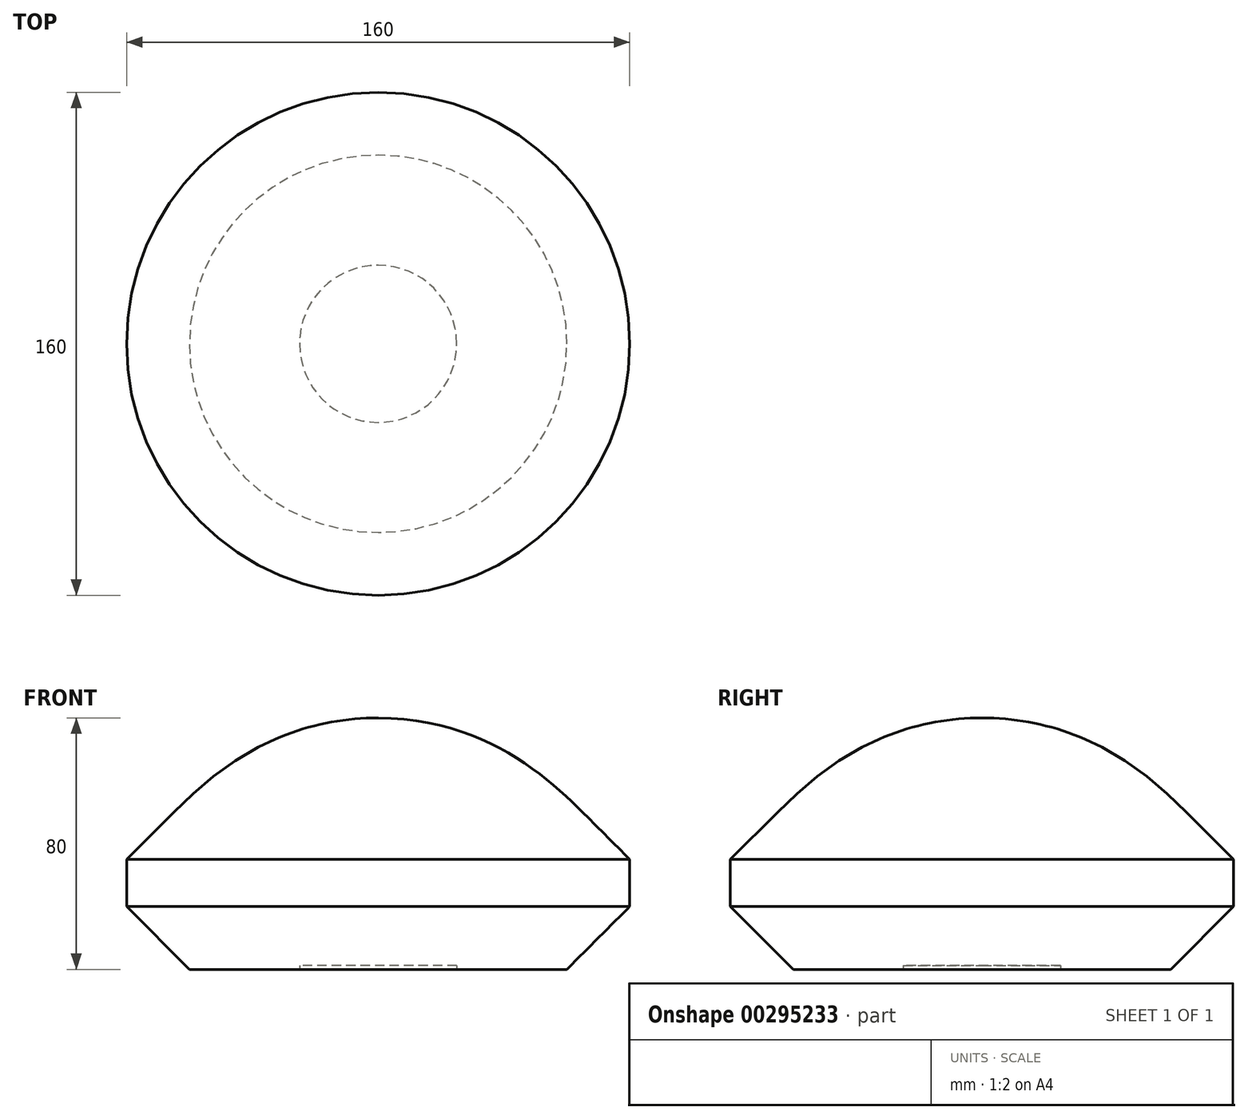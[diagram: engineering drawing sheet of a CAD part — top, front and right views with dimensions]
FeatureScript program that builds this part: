
annotation { "Feature Type Name" : "Feature", "Feature Type Description" : "" }
export const myFeature = defineFeature(function(context is Context, id is Id, definition is map)
    precondition{}
    {
        {
            var Q0;
            Q0=qCreatedBy(makeId("Front.planeOp"),FACE);
            var sketch = newSketch(context, id + "F0", { "sketchPlane" : qUnion([Q0])});
            skLineSegment(sketch, "E0", {"start": v(0, 0) * mm, "end": v(60, 0) * mm});
            skLineSegment(sketch, "E1", {"start": v(60, 0) * mm, "end": v(80, 20) * mm});
            skLineSegment(sketch, "E2", {"start": v(80, 20) * mm, "end": v(80, 35) * mm});
            skLineSegment(sketch, "E3", {"start": v(80, 35) * mm, "end": v(65, 50) * mm});
            skFitSpline(sketch, "E4", {"points": [v(0, 80) * mm, v(65, 50) * mm], "startDerivative": vector(97.72, -0.6) * mm, "endDerivative": vector(37.7, -37.7) * mm});
            skLineSegment(sketch, "E5", {"start": v(0, 80) * mm, "end": v(0, 0) * mm, "construction": true});
            skLineSegment(sketch, "E6", {"start": v(0, 80) * mm, "end": v(0, 0) * mm});
            skSolve(sketch);
        }
        {
            var Q0;
            Q0 = qSketchRegion(id + "F0", true);
            var Q1;
            Q1=sQuery(id+"F0.wireOp",EDGE,"E5");
            revolve(context, id + "F1", {"entities" : qUnion([Q0]), "axis" : qUnion([Q1]), "revolveType" : RevolveType.FULL});
        }
        {
            var Q0;
            Q0=qCreatedBy(makeId("Top.planeOp"),FACE);
            var sketch = newSketch(context, id + "F2", { "sketchPlane" : qUnion([Q0])});
            skCircle(sketch, "E7", {"center": v(0, 0) * mm, "radius": 25 * mm});
            skSolve(sketch);
        }
        {
            var Q0;
            Q0 = qSketchRegion(id + "F2", true);
            extrude(context, id + "F3", {"entities" : qUnion([Q0]), "operationType" : NewBodyOperationType.REMOVE, "depth" : 1.2 * mm});
        }
    });
